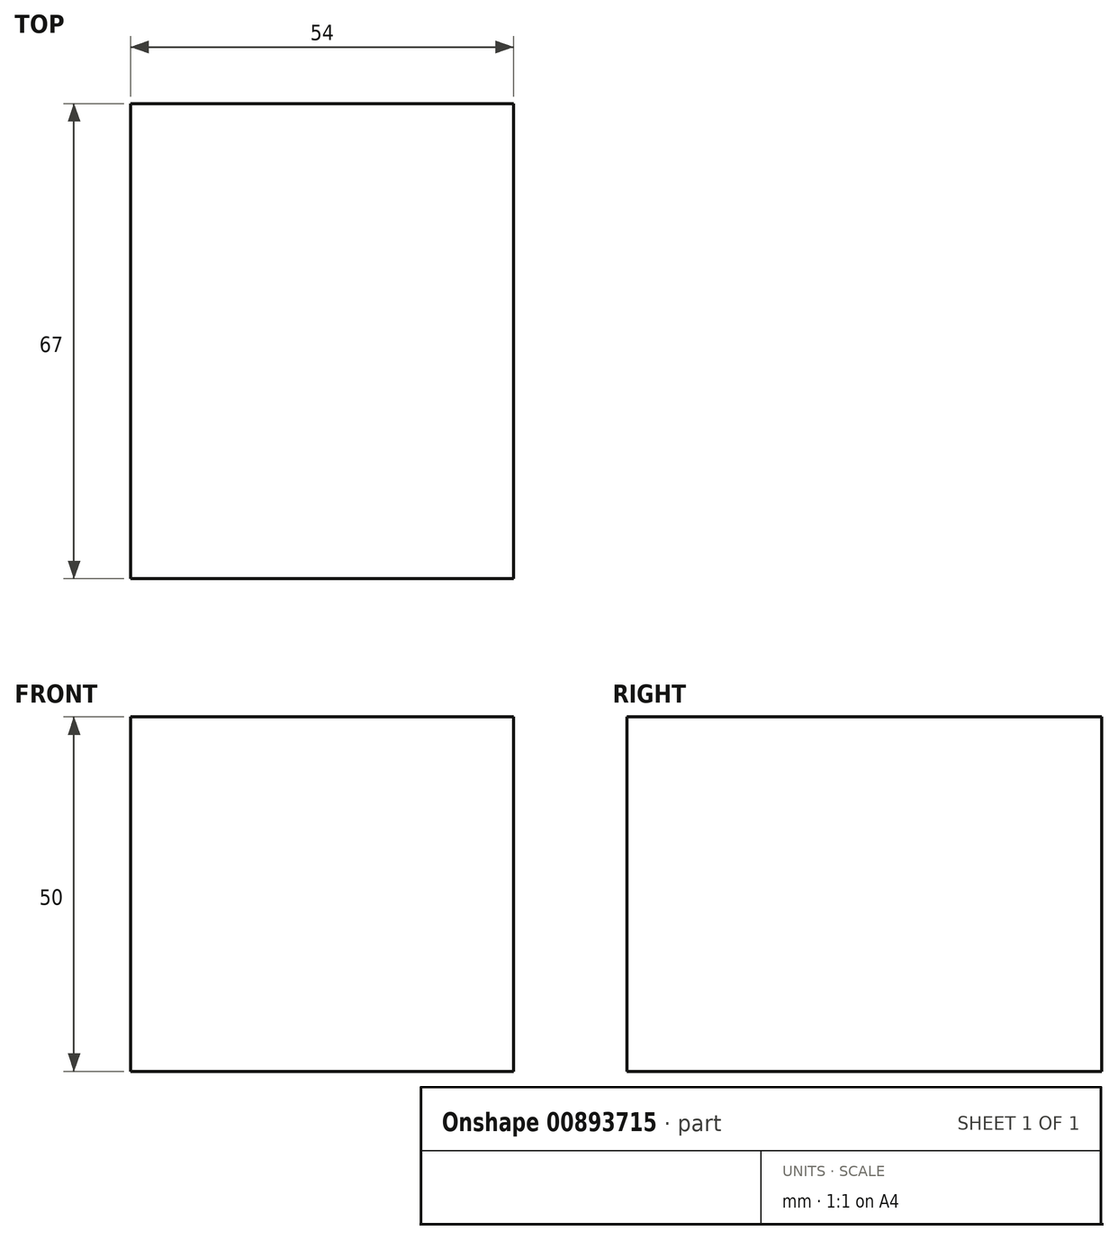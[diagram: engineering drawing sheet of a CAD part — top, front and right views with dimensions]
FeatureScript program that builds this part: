
annotation { "Feature Type Name" : "Feature", "Feature Type Description" : "" }
export const myFeature = defineFeature(function(context is Context, id is Id, definition is map)
    precondition{}
    {
        {
            var Q0;
            Q0=qCreatedBy(makeId("Top.planeOp"),FACE);
            var sketch = newSketch(context, id + "F0", { "sketchPlane" : qUnion([Q0])});
            skLineSegment(sketch, "E0.bottom", {"start": v(-23.91, 14.4) * mm, "end": v(30.09, 14.4) * mm});
            skLineSegment(sketch, "E0.top", {"start": v(-23.91, -52.6) * mm, "end": v(30.09, -52.6) * mm});
            skLineSegment(sketch, "E0.left", {"start": v(-23.91, 14.4) * mm, "end": v(-23.91, -52.6) * mm});
            skLineSegment(sketch, "E0.right", {"start": v(30.09, 14.4) * mm, "end": v(30.09, -52.6) * mm});
            skSolve(sketch);
        }
        {
            var Q0;
            Q0=makeQuery(id+"F0.imprint","IMPRINT",FACE,{"disambiguationData":[TD([[makeQuery(id+"F0.imprint","IMPRINT",EDGE,{"derivedFrom":sQuery(id+"F0.wireOp",EDGE,"E0.bottom")}),-1.0]])]});
            extrude(context, id + "F1", {"entities" : qUnion([Q0]), "depth" : 50 * mm, "offsetDistance" : 25 * mm});
        }
    });
